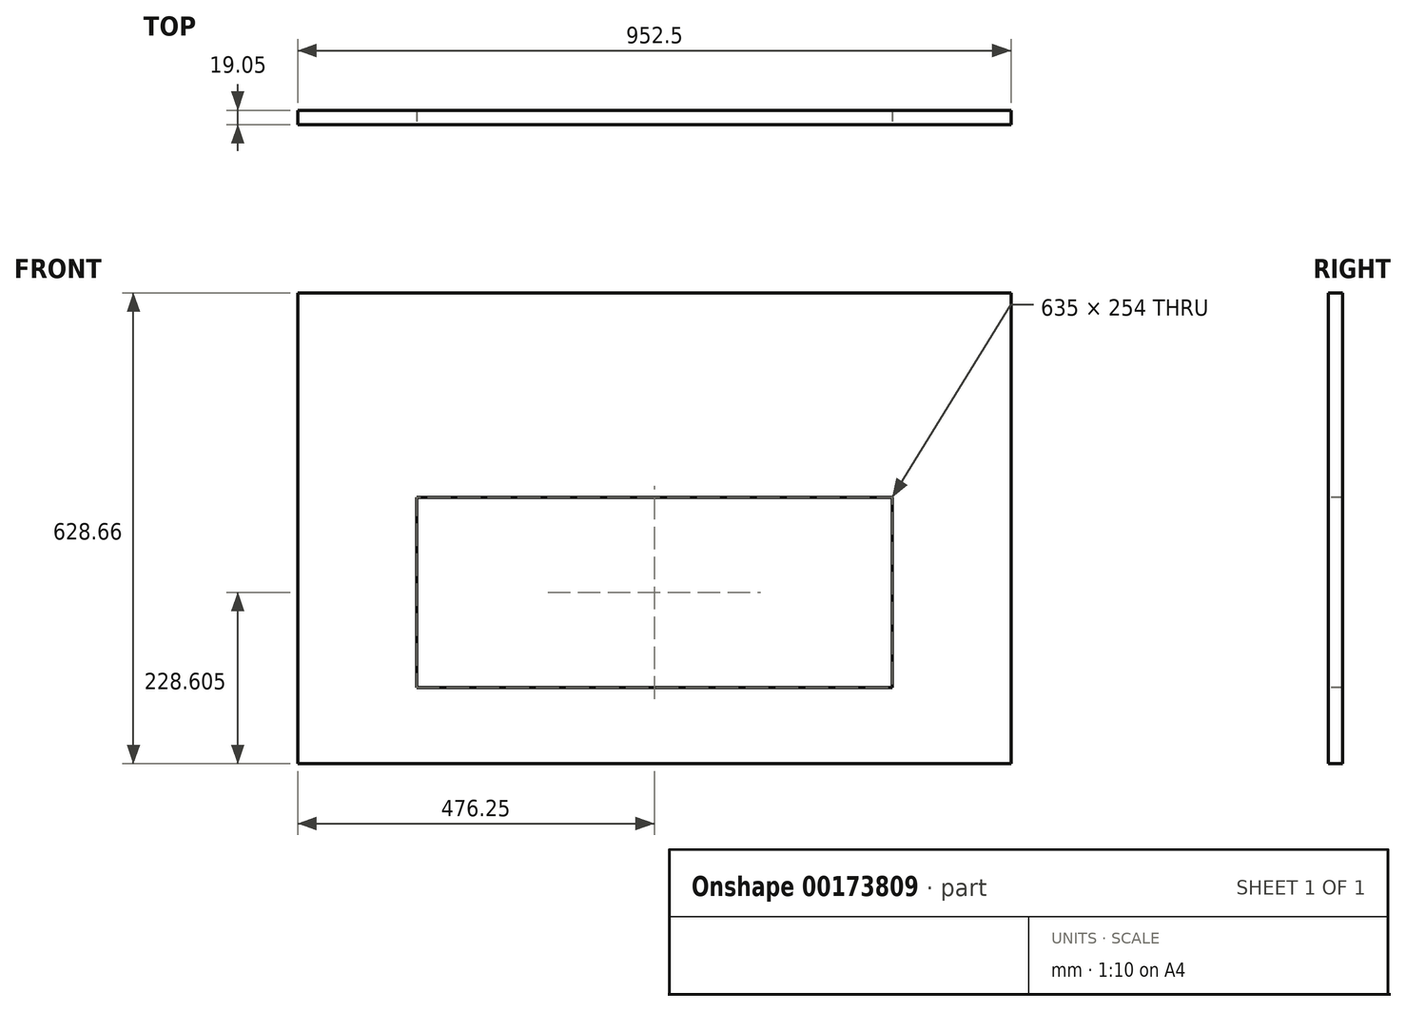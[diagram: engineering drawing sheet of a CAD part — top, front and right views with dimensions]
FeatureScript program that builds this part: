
annotation { "Feature Type Name" : "Feature", "Feature Type Description" : "" }
export const myFeature = defineFeature(function(context is Context, id is Id, definition is map)
    precondition{}
    {
        {
            var Q0;
            Q0=qCreatedBy(makeId("Front.planeOp"),FACE);
            var sketch = newSketch(context, id + "F0", { "sketchPlane" : qUnion([Q0])});
            skLineSegment(sketch, "E0.bottom", {"start": v(476.25, 314.33) * mm, "end": v(-476.25, 314.33) * mm});
            skLineSegment(sketch, "E0.top", {"start": v(476.25, -314.33) * mm, "end": v(-476.25, -314.33) * mm});
            skLineSegment(sketch, "E0.left", {"start": v(476.25, 314.33) * mm, "end": v(476.25, -314.33) * mm});
            skLineSegment(sketch, "E0.right", {"start": v(-476.25, 314.33) * mm, "end": v(-476.25, -314.33) * mm});
            skPoint(sketch, "E0.middle", {"position": v(0, 0) * mm});
            skSolve(sketch);
        }
        {
            var Q0;
            Q0 = qSketchRegion(id + "F0", true);
            extrude(context, id + "F1", {"entities" : qUnion([Q0]), "depth" : 19.05 * mm});
        }
        {
            var Q0;
            Q0=makeQuery(id+"F1.opExtrude","CAP_FACE",FACE,{"disambiguationData":[OSD([sQuery(id+"F0.wireOp",EDGE,"E0.bottom"),sQuery(id+"F0.wireOp",EDGE,"E0.top"),sQuery(id+"F0.wireOp",EDGE,"E0.left"),sQuery(id+"F0.wireOp",EDGE,"E0.right")])],"isStart":false});
            var sketch = newSketch(context, id + "F2", { "sketchPlane" : qUnion([Q0])});
            skLineSegment(sketch, "E1.bottom", {"start": v(317.5, 41.28) * mm, "end": v(-317.5, 41.27) * mm});
            skLineSegment(sketch, "E1.top", {"start": v(317.5, -212.73) * mm, "end": v(-317.5, -212.73) * mm});
            skLineSegment(sketch, "E1.left", {"start": v(317.5, 41.28) * mm, "end": v(317.5, -212.72) * mm});
            skLineSegment(sketch, "E1.right", {"start": v(-317.5, 41.27) * mm, "end": v(-317.5, -212.73) * mm});
            skPoint(sketch, "E1.middle", {"position": v(0, -85.73) * mm});
            skLineSegment(sketch, "E2", {"start": v(0, 0) * mm, "end": v(0, -85.73) * mm, "construction": true});
            skSolve(sketch);
        }
        {
            var Q0;
            Q0 = qSketchRegion(id + "F2", true);
            extrude(context, id + "F3", {"entities" : qUnion([Q0]), "operationType" : NewBodyOperationType.REMOVE, "endBound" : BoundingType.THROUGH_ALL, "oppositeDirection" : true, "depth" : 25.4 * mm});
        }
    });
